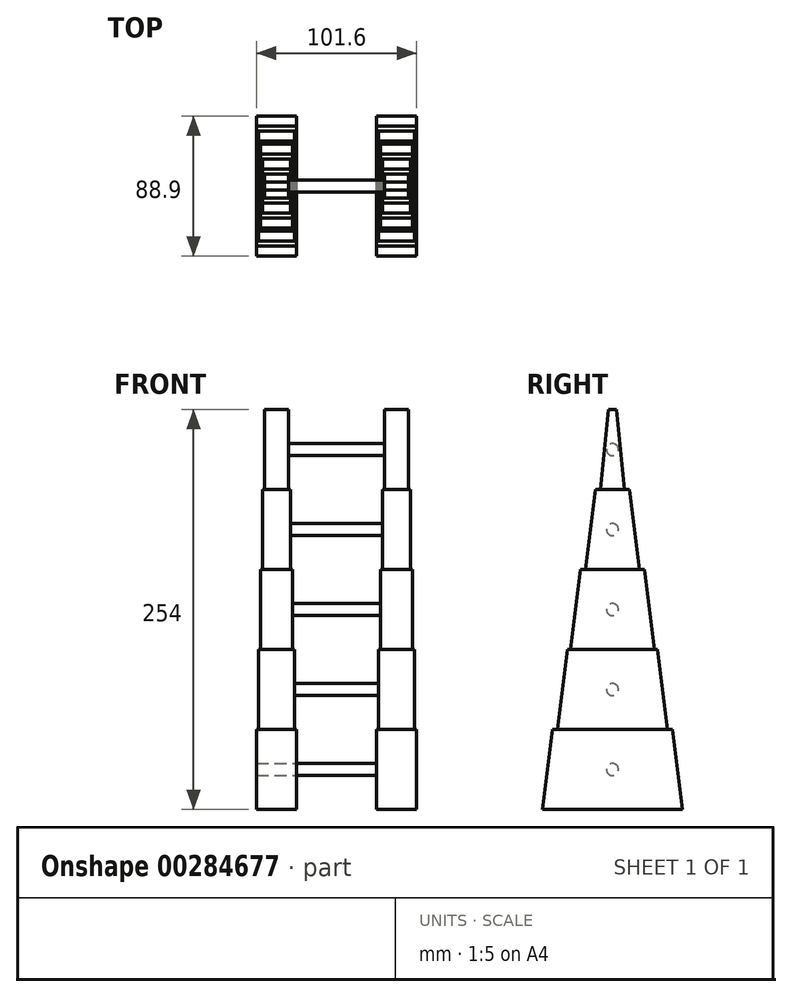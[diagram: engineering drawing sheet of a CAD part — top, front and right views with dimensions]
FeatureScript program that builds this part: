
annotation { "Feature Type Name" : "Feature", "Feature Type Description" : "" }
export const myFeature = defineFeature(function(context is Context, id is Id, definition is map)
    precondition{}
    {
        {
            var Q0;
            Q0=qCreatedBy(makeId("Top.planeOp"),FACE);
            var sketch = newSketch(context, id + "F0", { "sketchPlane" : qUnion([Q0])});
            skLineSegment(sketch, "E0.bottom", {"start": v(-50.8, 44.45) * mm, "end": v(-25.4, 44.45) * mm});
            skLineSegment(sketch, "E0.top", {"start": v(-50.8, -44.45) * mm, "end": v(-25.4, -44.45) * mm});
            skLineSegment(sketch, "E0.left", {"start": v(-50.8, 44.45) * mm, "end": v(-50.8, -44.45) * mm});
            skLineSegment(sketch, "E0.right", {"start": v(-25.4, 44.45) * mm, "end": v(-25.4, -44.45) * mm});
            skLineSegment(sketch, "E1.bottom", {"start": v(25.4, 44.45) * mm, "end": v(50.8, 44.45) * mm});
            skLineSegment(sketch, "E1.top", {"start": v(25.4, -44.45) * mm, "end": v(50.8, -44.45) * mm});
            skLineSegment(sketch, "E1.left", {"start": v(25.4, 44.45) * mm, "end": v(25.4, -44.45) * mm});
            skLineSegment(sketch, "E1.right", {"start": v(50.8, 44.45) * mm, "end": v(50.8, -44.45) * mm});
            skSolve(sketch);
        }
        {
            var Q0;
            Q0=makeQuery(id+"F0.imprint","IMPRINT",FACE,{"disambiguationData":[TD([[makeQuery(id+"F0.imprint","IMPRINT",EDGE,{"derivedFrom":sQuery(id+"F0.wireOp",EDGE,"E0.bottom")}),-1.0]])]});
            var Q1;
            Q1=makeQuery(id+"F0.imprint","IMPRINT",FACE,{"disambiguationData":[TD([[makeQuery(id+"F0.imprint","IMPRINT",EDGE,{"derivedFrom":sQuery(id+"F0.wireOp",EDGE,"E1.bottom")}),-1.0]])]});
            extrude(context, id + "F1", {"entities" : qUnion([Q0, Q1]), "depth" : 50.8 * mm});
        }
        {
            var Q0;
            Q0=makeQuery(id+"F1.opExtrude","CAP_EDGE",EDGE,{"disambiguationData":[OSD([sQuery(id+"F0.wireOp",EDGE,"E0.bottom")])],"isStart":false});
            var Q1;
            Q1=makeQuery(id+"F1.opExtrude","CAP_EDGE",EDGE,{"disambiguationData":[OSD([sQuery(id+"F0.wireOp",EDGE,"E1.bottom")])],"isStart":false});
            var Q2;
            Q2=makeQuery(id+"F1.opExtrude","CAP_EDGE",EDGE,{"disambiguationData":[OSD([sQuery(id+"F0.wireOp",EDGE,"E1.top")])],"isStart":false});
            var Q3;
            Q3=makeQuery(id+"F1.opExtrude","CAP_EDGE",EDGE,{"disambiguationData":[OSD([sQuery(id+"F0.wireOp",EDGE,"E0.top")])],"isStart":false});
            chamfer(context, id + "F2", {"entities" : qUnion([Q0, Q1, Q2, Q3]), "chamferType" : ChamferType.TWO_OFFSETS, "width1" : 50.8 * mm, "oppositeDirection" : false, "width2" : 6.35 * mm, "tangentPropagation" : true});
        }
        {
            var Q0;
            Q0=qCreatedBy(makeId("Top.planeOp"),FACE);
            cPlane(context, id + "F3", {"entities" : qUnion([Q0]), "cplaneType" : CPlaneType.OFFSET, "offset" : 50.8 * mm, "width" : 152.4 * mm, "height" : 152.4 * mm});
        }
        {
            var Q0;
            Q0=qCreatedBy(id+"F3.planeOp",FACE);
            var sketch = newSketch(context, id + "F4", { "sketchPlane" : qUnion([Q0])});
            skLineSegment(sketch, "E2.bottom", {"start": v(-49.53, 34.93) * mm, "end": v(-26.67, 34.93) * mm});
            skLineSegment(sketch, "E2.top", {"start": v(-49.53, -34.93) * mm, "end": v(-26.67, -34.93) * mm});
            skLineSegment(sketch, "E2.left", {"start": v(-49.53, 34.93) * mm, "end": v(-49.53, -34.93) * mm});
            skLineSegment(sketch, "E2.right", {"start": v(-26.67, 34.93) * mm, "end": v(-26.67, -34.93) * mm});
            skLineSegment(sketch, "E3.bottom", {"start": v(26.67, 34.93) * mm, "end": v(49.53, 34.93) * mm});
            skLineSegment(sketch, "E3.top", {"start": v(26.67, -34.93) * mm, "end": v(49.53, -34.93) * mm});
            skLineSegment(sketch, "E3.left", {"start": v(26.67, 34.93) * mm, "end": v(26.67, -34.93) * mm});
            skLineSegment(sketch, "E3.right", {"start": v(49.53, 34.93) * mm, "end": v(49.53, -34.93) * mm});
            skSolve(sketch);
        }
        {
            var Q0;
            Q0 = qSketchRegion(id + "F4", true);
            extrude(context, id + "F5", {"entities" : qUnion([Q0]), "depth" : 50.8 * mm});
        }
        {
            var Q0;
            Q0=makeQuery(id+"F5.opExtrude","CAP_EDGE",EDGE,{"disambiguationData":[OSD([sQuery(id+"F4.wireOp",EDGE,"E2.bottom")])],"isStart":false});
            var Q1;
            Q1=makeQuery(id+"F5.opExtrude","CAP_EDGE",EDGE,{"disambiguationData":[OSD([sQuery(id+"F4.wireOp",EDGE,"E3.bottom")])],"isStart":false});
            var Q2;
            Q2=makeQuery(id+"F5.opExtrude","CAP_EDGE",EDGE,{"disambiguationData":[OSD([sQuery(id+"F4.wireOp",EDGE,"E2.top")])],"isStart":false});
            var Q3;
            Q3=makeQuery(id+"F5.opExtrude","CAP_EDGE",EDGE,{"disambiguationData":[OSD([sQuery(id+"F4.wireOp",EDGE,"E3.top")])],"isStart":false});
            chamfer(context, id + "F6", {"entities" : qUnion([Q0, Q1, Q2, Q3]), "chamferType" : ChamferType.TWO_OFFSETS, "width1" : 50.8 * mm, "oppositeDirection" : false, "width2" : 6.35 * mm, "tangentPropagation" : true});
        }
        {
            var Q0;
            Q0=qCreatedBy(id+"F3.planeOp",FACE);
            cPlane(context, id + "F7", {"entities" : qUnion([Q0]), "cplaneType" : CPlaneType.OFFSET, "offset" : 50.8 * mm, "width" : 152.4 * mm, "height" : 152.4 * mm});
        }
        {
            var Q0;
            Q0=qCreatedBy(id+"F7.planeOp",FACE);
            var sketch = newSketch(context, id + "F8", { "sketchPlane" : qUnion([Q0])});
            skLineSegment(sketch, "E4.bottom", {"start": v(-48.26, 26.67) * mm, "end": v(-27.94, 26.67) * mm});
            skLineSegment(sketch, "E4.top", {"start": v(-48.26, -26.67) * mm, "end": v(-27.94, -26.67) * mm});
            skLineSegment(sketch, "E4.left", {"start": v(-48.26, 26.67) * mm, "end": v(-48.26, -26.67) * mm});
            skLineSegment(sketch, "E4.right", {"start": v(-27.94, 26.67) * mm, "end": v(-27.94, -26.67) * mm});
            skLineSegment(sketch, "E5.bottom", {"start": v(27.94, 26.67) * mm, "end": v(48.26, 26.67) * mm});
            skLineSegment(sketch, "E5.top", {"start": v(27.94, -26.67) * mm, "end": v(48.26, -26.67) * mm});
            skLineSegment(sketch, "E5.left", {"start": v(27.94, 26.67) * mm, "end": v(27.94, -26.67) * mm});
            skLineSegment(sketch, "E5.right", {"start": v(48.26, 26.67) * mm, "end": v(48.26, -26.67) * mm});
            skSolve(sketch);
        }
        {
            var Q0;
            Q0 = qSketchRegion(id + "F8", true);
            extrude(context, id + "F9", {"entities" : qUnion([Q0]), "depth" : 50.8 * mm});
        }
        {
            var Q0;
            Q0=makeQuery(id+"F9.opExtrude","CAP_EDGE",EDGE,{"disambiguationData":[OSD([sQuery(id+"F8.wireOp",EDGE,"E4.bottom")])],"isStart":false});
            var Q1;
            Q1=makeQuery(id+"F9.opExtrude","CAP_EDGE",EDGE,{"disambiguationData":[OSD([sQuery(id+"F8.wireOp",EDGE,"E5.bottom")])],"isStart":false});
            var Q2;
            Q2=makeQuery(id+"F9.opExtrude","CAP_EDGE",EDGE,{"disambiguationData":[OSD([sQuery(id+"F8.wireOp",EDGE,"E5.top")])],"isStart":false});
            var Q3;
            Q3=makeQuery(id+"F9.opExtrude","CAP_EDGE",EDGE,{"disambiguationData":[OSD([sQuery(id+"F8.wireOp",EDGE,"E4.top")])],"isStart":false});
            chamfer(context, id + "F10", {"entities" : qUnion([Q0, Q1, Q2, Q3]), "chamferType" : ChamferType.TWO_OFFSETS, "width1" : 50.8 * mm, "oppositeDirection" : false, "width2" : 6.35 * mm, "tangentPropagation" : true});
        }
        {
            var Q0;
            Q0=qCreatedBy(id+"F7.planeOp",FACE);
            cPlane(context, id + "F11", {"entities" : qUnion([Q0]), "cplaneType" : CPlaneType.OFFSET, "offset" : 50.8 * mm, "width" : 152.4 * mm, "height" : 152.4 * mm});
        }
        {
            var Q0;
            Q0=qCreatedBy(id+"F11.planeOp",FACE);
            var sketch = newSketch(context, id + "F12", { "sketchPlane" : qUnion([Q0])});
            skLineSegment(sketch, "E6.bottom", {"start": v(-47, 17.02) * mm, "end": v(-29.21, 17.02) * mm});
            skLineSegment(sketch, "E6.top", {"start": v(-47, -17.27) * mm, "end": v(-29.21, -17.27) * mm});
            skLineSegment(sketch, "E6.left", {"start": v(-47, 17.02) * mm, "end": v(-47, -17.27) * mm});
            skLineSegment(sketch, "E6.right", {"start": v(-29.21, 17.02) * mm, "end": v(-29.21, -17.27) * mm});
            skLineSegment(sketch, "E7.bottom", {"start": v(29.21, 17.02) * mm, "end": v(47, 17.02) * mm});
            skLineSegment(sketch, "E7.top", {"start": v(29.21, -17.27) * mm, "end": v(47, -17.27) * mm});
            skLineSegment(sketch, "E7.left", {"start": v(29.21, 17.02) * mm, "end": v(29.21, -17.27) * mm});
            skLineSegment(sketch, "E7.right", {"start": v(47, 17.02) * mm, "end": v(47, -17.27) * mm});
            skSolve(sketch);
        }
        {
            var Q0;
            Q0 = qSketchRegion(id + "F12", true);
            extrude(context, id + "F13", {"entities" : qUnion([Q0]), "depth" : 50.8 * mm});
        }
        {
            var Q0;
            Q0=makeQuery(id+"F13.opExtrude","CAP_EDGE",EDGE,{"disambiguationData":[OSD([sQuery(id+"F12.wireOp",EDGE,"E6.bottom")])],"isStart":false});
            var Q1;
            Q1=makeQuery(id+"F13.opExtrude","CAP_EDGE",EDGE,{"disambiguationData":[OSD([sQuery(id+"F12.wireOp",EDGE,"E7.bottom")])],"isStart":false});
            var Q2;
            Q2=makeQuery(id+"F13.opExtrude","CAP_EDGE",EDGE,{"disambiguationData":[OSD([sQuery(id+"F12.wireOp",EDGE,"E6.top")])],"isStart":false});
            var Q3;
            Q3=makeQuery(id+"F13.opExtrude","CAP_EDGE",EDGE,{"disambiguationData":[OSD([sQuery(id+"F12.wireOp",EDGE,"E7.top")])],"isStart":false});
            chamfer(context, id + "F14", {"entities" : qUnion([Q0, Q1, Q2, Q3]), "chamferType" : ChamferType.TWO_OFFSETS, "width1" : 50.8 * mm, "oppositeDirection" : false, "width2" : 6.35 * mm, "tangentPropagation" : true});
        }
        {
            var Q0;
            Q0=qCreatedBy(id+"F11.planeOp",FACE);
            cPlane(context, id + "F15", {"entities" : qUnion([Q0]), "cplaneType" : CPlaneType.OFFSET, "offset" : 50.8 * mm, "width" : 152.4 * mm, "height" : 152.4 * mm});
        }
        {
            var Q0;
            Q0=qCreatedBy(id+"F15.planeOp",FACE);
            var sketch = newSketch(context, id + "F16", { "sketchPlane" : qUnion([Q0])});
            skLineSegment(sketch, "E8.bottom", {"start": v(-45.72, 7.62) * mm, "end": v(-30.48, 7.62) * mm});
            skLineSegment(sketch, "E8.top", {"start": v(-45.72, -7.62) * mm, "end": v(-30.48, -7.62) * mm});
            skLineSegment(sketch, "E8.left", {"start": v(-45.72, 7.62) * mm, "end": v(-45.72, -7.62) * mm});
            skLineSegment(sketch, "E8.right", {"start": v(-30.48, 7.62) * mm, "end": v(-30.48, -7.62) * mm});
            skLineSegment(sketch, "E9.bottom", {"start": v(30.48, 7.62) * mm, "end": v(45.72, 7.62) * mm});
            skLineSegment(sketch, "E9.top", {"start": v(30.48, -7.62) * mm, "end": v(45.72, -7.62) * mm});
            skLineSegment(sketch, "E9.left", {"start": v(30.48, 7.62) * mm, "end": v(30.48, -7.62) * mm});
            skLineSegment(sketch, "E9.right", {"start": v(45.72, 7.62) * mm, "end": v(45.72, -7.62) * mm});
            skSolve(sketch);
        }
        {
            var Q0;
            Q0 = qSketchRegion(id + "F16", true);
            extrude(context, id + "F17", {"entities" : qUnion([Q0]), "depth" : 50.8 * mm});
        }
        {
            var Q0;
            Q0=makeQuery(id+"F17.opExtrude","CAP_EDGE",EDGE,{"disambiguationData":[OSD([sQuery(id+"F16.wireOp",EDGE,"E8.bottom")])],"isStart":false});
            var Q1;
            Q1=makeQuery(id+"F17.opExtrude","CAP_EDGE",EDGE,{"disambiguationData":[OSD([sQuery(id+"F16.wireOp",EDGE,"E9.bottom")])],"isStart":false});
            var Q2;
            Q2=makeQuery(id+"F17.opExtrude","CAP_EDGE",EDGE,{"disambiguationData":[OSD([sQuery(id+"F16.wireOp",EDGE,"E8.top")])],"isStart":false});
            var Q3;
            Q3=makeQuery(id+"F17.opExtrude","CAP_EDGE",EDGE,{"disambiguationData":[OSD([sQuery(id+"F16.wireOp",EDGE,"E9.top")])],"isStart":false});
            chamfer(context, id + "F18", {"entities" : qUnion([Q0, Q1, Q2, Q3]), "chamferType" : ChamferType.TWO_OFFSETS, "width1" : 50.8 * mm, "oppositeDirection" : false, "width2" : 5.08 * mm, "tangentPropagation" : true});
        }
        {
            var Q0;
            Q0=makeQuery(id+"F1.opExtrude","SWEPT_FACE",FACE,{"disambiguationData":[OSD([sQuery(id+"F0.wireOp",EDGE,"E0.right")])]});
            var sketch = newSketch(context, id + "F19", { "sketchPlane" : qUnion([Q0])});
            skCircle(sketch, "E10", {"center": v(0, 228.6) * mm, "radius": 3.81 * mm});
            skCircle(sketch, "E11.MirrorC", {"center": v(0, 177.8) * mm, "radius": 3.81 * mm});
            skCircle(sketch, "E12.MirrorC", {"center": v(0, 127) * mm, "radius": 3.81 * mm});
            skCircle(sketch, "E13.MirrorC", {"center": v(0, 76.2) * mm, "radius": 3.81 * mm});
            skCircle(sketch, "E14.MirrorC", {"center": v(0, 25.4) * mm, "radius": 3.81 * mm});
            skSolve(sketch);
        }
        {
            var Q0;
            Q0 = qSketchRegion(id + "F19", true);
            extrude(context, id + "F20", {"entities" : qUnion([Q0]), "endBound" : BoundingType.UP_TO_NEXT, "oppositeDirection" : true, "depth" : 50.8 * mm, "hasSecondDirection" : true, "secondDirectionBound" : SecondDirectionBoundingType.UP_TO_NEXT, "secondDirectionOppositeDirection" : false, "secondDirectionDepth" : 50.8 * mm});
        }
    });
